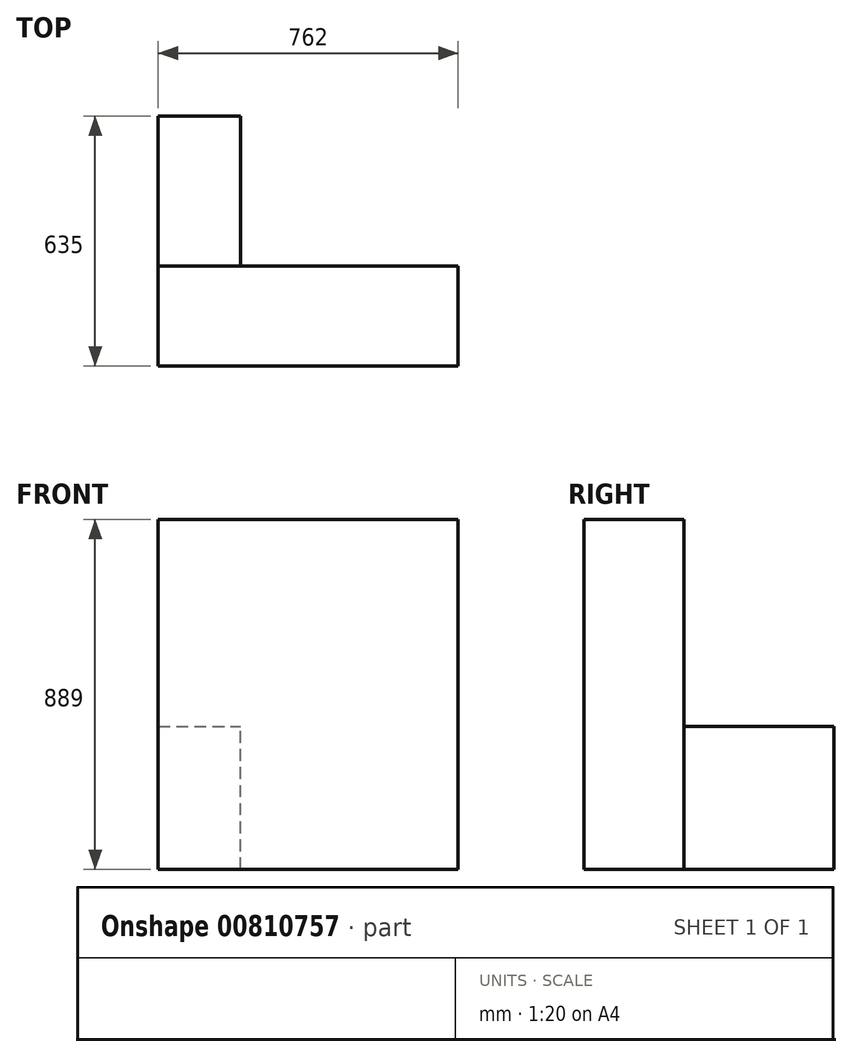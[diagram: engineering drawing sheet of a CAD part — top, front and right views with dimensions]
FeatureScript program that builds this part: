
annotation { "Feature Type Name" : "Feature", "Feature Type Description" : "" }
export const myFeature = defineFeature(function(context is Context, id is Id, definition is map)
    precondition{}
    {
        {
            var Q0;
            Q0=qCreatedBy(makeId("Top.planeOp"),FACE);
            var sketch = newSketch(context, id + "F0", { "sketchPlane" : qUnion([Q0])});
            skLineSegment(sketch, "E0.bottom", {"start": v(-375.87, 43.56) * mm, "end": v(386.13, 43.56) * mm});
            skLineSegment(sketch, "E0.top", {"start": v(-375.87, -210.44) * mm, "end": v(386.13, -210.44) * mm});
            skLineSegment(sketch, "E0.left", {"start": v(-375.87, 43.56) * mm, "end": v(-375.87, -210.44) * mm});
            skLineSegment(sketch, "E0.right", {"start": v(386.13, 43.56) * mm, "end": v(386.13, -210.44) * mm});
            skSolve(sketch);
        }
        {
            var Q0;
            Q0 = qSketchRegion(id + "F0", true);
            extrude(context, id + "F1", {"entities" : qUnion([Q0]), "depth" : 889 * mm, "offsetDistance" : 25.4 * mm});
        }
        {
            var Q0;
            Q0=makeQuery(id+"F1.opExtrude","SWEPT_FACE",FACE,{"disambiguationData":[OSD([sQuery(id+"F0.wireOp",EDGE,"E0.bottom")])]});
            var sketch = newSketch(context, id + "F2", { "sketchPlane" : qUnion([Q0])});
            skLineSegment(sketch, "E1.bottom", {"start": v(375.87, 0) * mm, "end": v(167.1, 0) * mm});
            skLineSegment(sketch, "E1.top", {"start": v(375.87, 363.57) * mm, "end": v(167.1, 363.57) * mm});
            skLineSegment(sketch, "E1.left", {"start": v(375.87, 0) * mm, "end": v(375.87, 363.57) * mm});
            skLineSegment(sketch, "E1.right", {"start": v(167.1, 0) * mm, "end": v(167.1, 363.57) * mm});
            skSolve(sketch);
        }
        {
            var Q0;
            Q0=makeQuery(id+"F2.imprint","IMPRINT",FACE,{"disambiguationData":[TD([[makeQuery(id+"F2.imprint","IMPRINT",EDGE,{"derivedFrom":sQuery(id+"F2.wireOp",EDGE,"E1.bottom")}),-1.0]])]});
            extrude(context, id + "F3", {"entities" : qUnion([Q0]), "operationType" : NewBodyOperationType.ADD, "depth" : 381 * mm, "offsetDistance" : 25.4 * mm});
        }
    });
